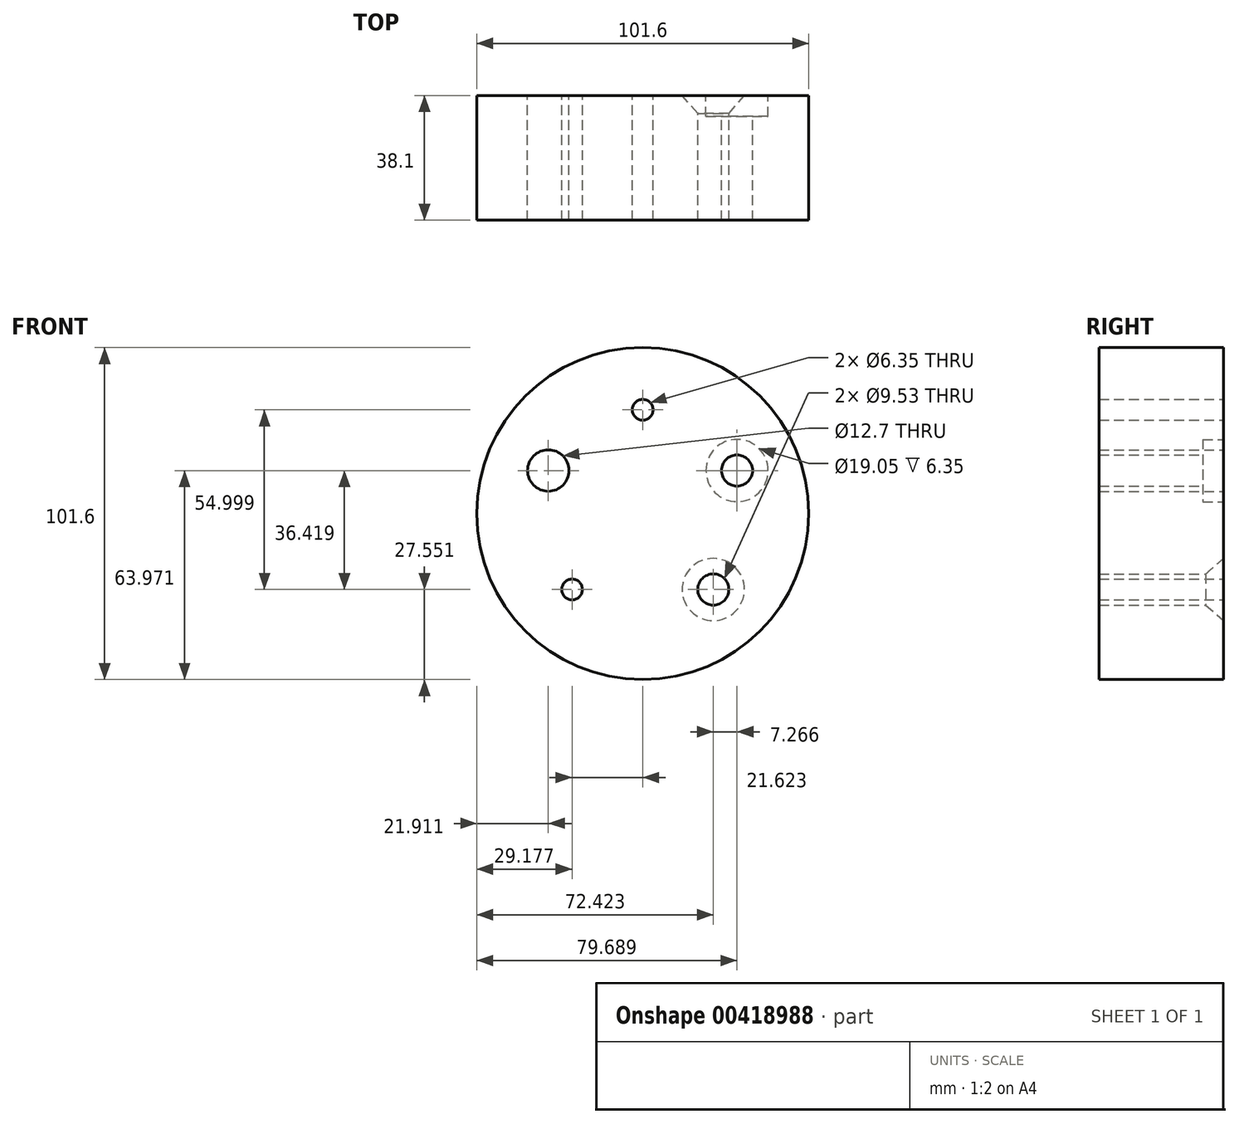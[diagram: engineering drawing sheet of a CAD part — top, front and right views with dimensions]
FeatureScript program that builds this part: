
annotation { "Feature Type Name" : "Feature", "Feature Type Description" : "" }
export const myFeature = defineFeature(function(context is Context, id is Id, definition is map)
    precondition{}
    {
        {
            var Q0;
            Q0=qCreatedBy(makeId("Front.planeOp"),FACE);
            var sketch = newSketch(context, id + "F0", { "sketchPlane" : qUnion([Q0])});
            skCircle(sketch, "E0", {"center": v(0, 0) * mm, "radius": 50.8 * mm});
            skSolve(sketch);
        }
        {
            var Q0;
            Q0=makeQuery(id+"F0.imprint","IMPRINT",FACE,{"disambiguationData":[TD([[makeQuery(id+"F0.imprint","IMPRINT",EDGE,{"derivedFrom":sQuery(id+"F0.wireOp",EDGE,"E0")}),1.0]])]});
            extrude(context, id + "F1", {"entities" : qUnion([Q0]), "depth" : 38.1 * mm});
        }
        {
            var Q0;
            Q0=qCreatedBy(makeId("Front.planeOp"),FACE);
            var sketch = newSketch(context, id + "F2", { "sketchPlane" : qUnion([Q0])});
            skPoint(sketch, "E1", {"position": v(0, 31.75) * mm});
            skPoint(sketch, "E2", {"position": v(28.89, 13.17) * mm});
            skPoint(sketch, "E3", {"position": v(21.62, -23.25) * mm});
            skPoint(sketch, "E4", {"position": v(-21.62, -23.25) * mm});
            skPoint(sketch, "E5", {"position": v(-28.89, 13.17) * mm});
            skSolve(sketch);
        }
        {
            var Q0;
            Q0=sQuery(id+"F2.wireOp",VERTEX,"E1");
            var Q1;
            Q1=makeQuery(id+"F1.opExtrude","SWEPT_BODY",BODY,{"disambiguationData":[OSD([sQuery(id+"F0.wireOp",EDGE,"E0")])]});
            hole(context, id + "F3", {"style" : HoleStyle.SIMPLE, "endStyle" : HoleEndStyle.THROUGH, "oppositeDirection" : true, "holeDiameter" : 6.35 * mm, "isTappedThrough" : true, "tappedDepth" : 12.7 * mm, "tapClearance" : 3, "locations" : qUnion([Q0]), "scope" : qUnion([Q1])});
        }
        {
            var Q0;
            Q0=sQuery(id+"F2.wireOp",VERTEX,"E5");
            var Q1;
            Q1=makeQuery(id+"F1.opExtrude","SWEPT_BODY",BODY,{"disambiguationData":[OSD([sQuery(id+"F0.wireOp",EDGE,"E0")])]});
            hole(context, id + "F4", {"style" : HoleStyle.SIMPLE, "endStyle" : HoleEndStyle.THROUGH, "oppositeDirection" : true, "holeDiameter" : 12.7 * mm, "isTappedThrough" : true, "tappedDepth" : 12.7 * mm, "tapClearance" : 3, "locations" : qUnion([Q0]), "scope" : qUnion([Q1])});
        }
        {
            var Q0;
            Q0=sQuery(id+"F2.wireOp",VERTEX,"E2");
            var Q1;
            Q1=makeQuery(id+"F1.opExtrude","SWEPT_BODY",BODY,{"disambiguationData":[OSD([sQuery(id+"F0.wireOp",EDGE,"E0")])]});
            hole(context, id + "F5", {"style" : HoleStyle.C_BORE, "endStyle" : HoleEndStyle.THROUGH, "oppositeDirection" : true, "holeDiameter" : 9.52 * mm, "cBoreDiameter" : 19.05 * mm, "cBoreDepth" : 6.35 * mm, "isTappedThrough" : true, "tappedDepth" : 12.7 * mm, "tapClearance" : 3, "locations" : qUnion([Q0]), "scope" : qUnion([Q1])});
        }
        {
            var Q0;
            Q0=sQuery(id+"F2.wireOp",VERTEX,"E3");
            var Q1;
            Q1=makeQuery(id+"F1.opExtrude","SWEPT_BODY",BODY,{"disambiguationData":[OSD([sQuery(id+"F0.wireOp",EDGE,"E0")])]});
            hole(context, id + "F6", {"style" : HoleStyle.C_SINK, "endStyle" : HoleEndStyle.THROUGH, "oppositeDirection" : true, "holeDiameter" : 9.52 * mm, "cSinkDiameter" : 19.05 * mm, "cSinkAngle" : 82 * degree, "isTappedThrough" : true, "tappedDepth" : 12.7 * mm, "tapClearance" : 3, "locations" : qUnion([Q0]), "scope" : qUnion([Q1])});
        }
        {
            var Q0;
            Q0=sQuery(id+"F2.wireOp",VERTEX,"E4");
            var Q1;
            Q1=makeQuery(id+"F1.opExtrude","SWEPT_BODY",BODY,{"disambiguationData":[OSD([sQuery(id+"F0.wireOp",EDGE,"E0")])]});
            hole(context, id + "F7", {"style" : HoleStyle.SIMPLE, "endStyle" : HoleEndStyle.THROUGH, "oppositeDirection" : true, "holeDiameter" : 6.35 * mm, "isTappedThrough" : true, "tappedDepth" : 12.7 * mm, "tapClearance" : 3, "locations" : qUnion([Q0]), "scope" : qUnion([Q1])});
        }
    });
